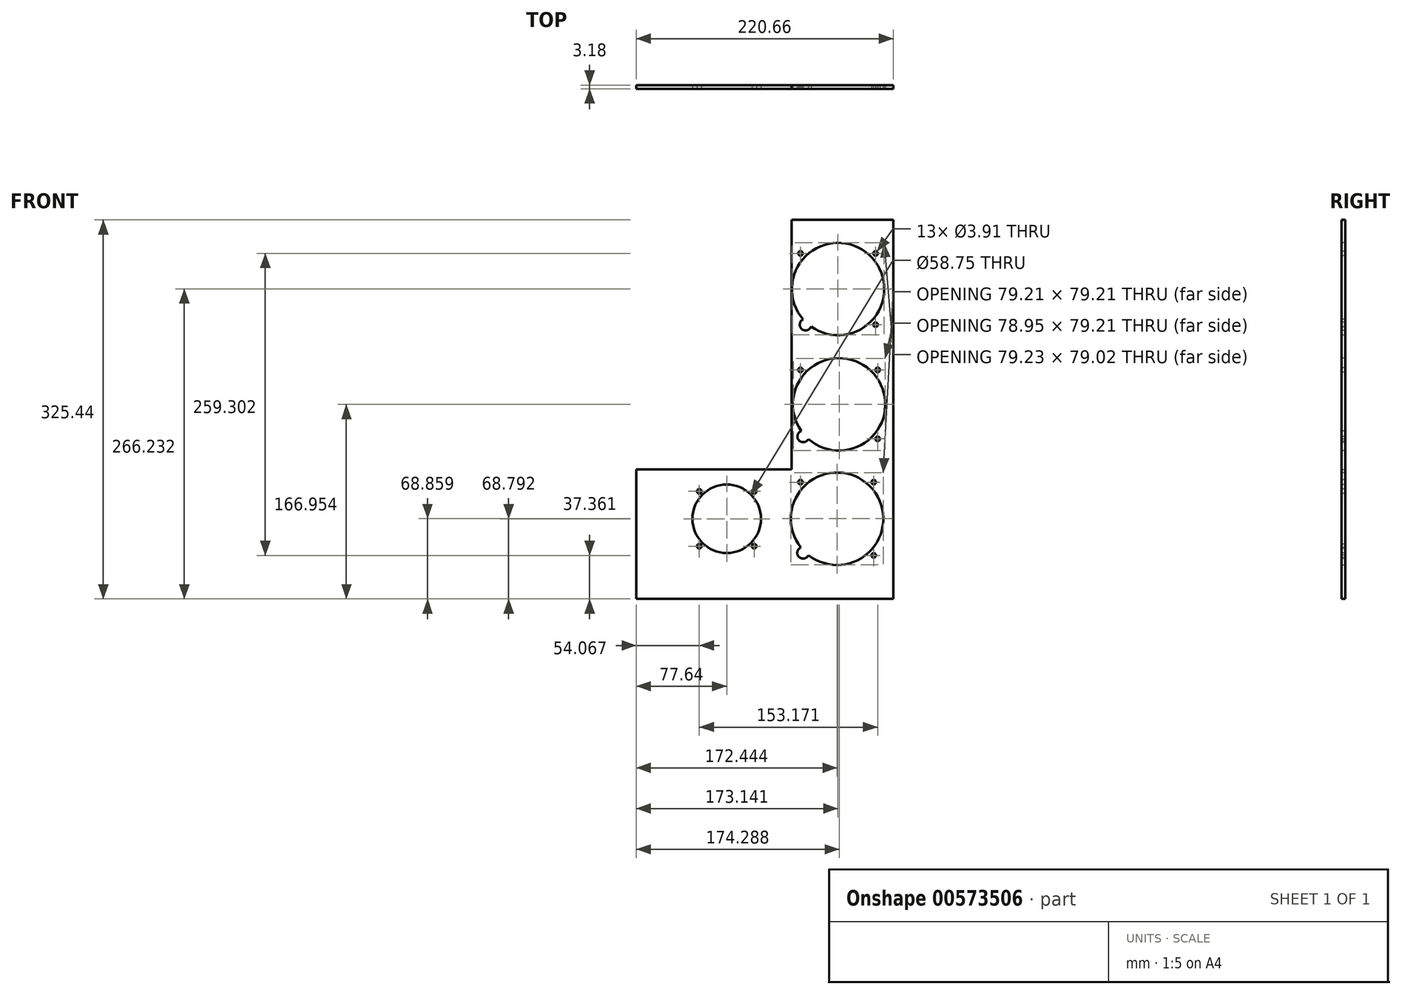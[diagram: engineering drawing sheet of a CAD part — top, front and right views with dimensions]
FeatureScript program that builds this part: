
annotation { "Feature Type Name" : "Feature", "Feature Type Description" : "" }
export const myFeature = defineFeature(function(context is Context, id is Id, definition is map)
    precondition{}
    {
        {
            var Q0;
            Q0=qCreatedBy(makeId("Front.planeOp"),FACE);
            var sketch = newSketch(context, id + "F0", { "sketchPlane" : qUnion([Q0])});
            skLineSegment(sketch, "E0", {"start": v(279.4, 0) * mm, "end": v(500.06, 0) * mm});
            skLineSegment(sketch, "E1", {"start": v(500.06, 0) * mm, "end": v(500.06, 325.44) * mm});
            skLineSegment(sketch, "E2", {"start": v(500.06, 325.44) * mm, "end": v(412.75, 325.44) * mm});
            skLineSegment(sketch, "E3", {"start": v(412.75, 325.44) * mm, "end": v(412.75, 111.13) * mm});
            skLineSegment(sketch, "E4", {"start": v(412.75, 111.13) * mm, "end": v(279.4, 111.13) * mm});
            skLineSegment(sketch, "E5", {"start": v(279.4, 111.12) * mm, "end": v(279.4, 0) * mm});
            skSolve(sketch);
        }
        {
            assignVariable(context, id + "F1", {"name" : "PanelThickness", "anyValue" : 3.17 * mm});
        }
        {
            var Q0;
            Q0=makeQuery(id+"F0.imprint","IMPRINT",FACE,{"disambiguationData":[TD([[makeQuery(id+"F0.imprint","IMPRINT",EDGE,{"derivedFrom":sQuery(id+"F0.wireOp",EDGE,"E0")}),1.0]])]});
            extrude(context, id + "F2", {"entities" : qUnion([Q0]), "depth" : (getVariable(context, 'PanelThickness')), "offsetDistance" : 25.4 * mm});
        }
        {
            var Q0;
            Q0=makeQuery(id+"F2.opExtrude","CAP_FACE",FACE,{"disambiguationData":[OSD([sQuery(id+"F0.wireOp",EDGE,"E0"),sQuery(id+"F0.wireOp",EDGE,"E1"),sQuery(id+"F0.wireOp",EDGE,"E2"),sQuery(id+"F0.wireOp",EDGE,"E3"),sQuery(id+"F0.wireOp",EDGE,"E4"),sQuery(id+"F0.wireOp",EDGE,"E5")])],"isStart":false});
            var sketch = newSketch(context, id + "F3", { "sketchPlane" : qUnion([Q0])});
            skCircle(sketch, "E6", {"center": v(452.58, 266.06) * mm, "radius": 39.69 * mm});
            skCircle(sketch, "E7.2.0.0", {"center": v(420.35, 296.66) * mm, "radius": 1.96 * mm});
            skCircle(sketch, "E7.2.0.1", {"center": v(484.82, 296.66) * mm, "radius": 1.96 * mm});
            skCircle(sketch, "E7.2.0.2", {"center": v(484.82, 235.45) * mm, "radius": 1.96 * mm});
            skLineSegment(sketch, "E8", {"start": v(484.82, 296.66) * mm, "end": v(424.73, 235.45) * mm});
            skCircle(sketch, "E9", {"center": v(424.73, 235.45) * mm, "radius": 4.97 * mm});
            skLineSegment(sketch, "E10", {"start": v(420.35, 296.66) * mm, "end": v(484.82, 235.45) * mm});
            skCircle(sketch, "E11", {"center": v(453.5, 167.02) * mm, "radius": 39.69 * mm});
            skCircle(sketch, "E12.2.0.0", {"center": v(420.35, 196.63) * mm, "radius": 1.96 * mm});
            skCircle(sketch, "E12.2.0.1", {"center": v(486.64, 196.63) * mm, "radius": 1.96 * mm});
            skCircle(sketch, "E12.2.0.2", {"center": v(486.64, 137.4) * mm, "radius": 1.96 * mm});
            skLineSegment(sketch, "E13", {"start": v(486.64, 196.63) * mm, "end": v(422.68, 139.48) * mm});
            skCircle(sketch, "E14", {"center": v(422.68, 139.48) * mm, "radius": 4.97 * mm});
            skLineSegment(sketch, "E15", {"start": v(420.35, 196.63) * mm, "end": v(486.64, 137.4) * mm});
            skCircle(sketch, "E16", {"center": v(451.78, 68.8) * mm, "radius": 39.69 * mm});
            skCircle(sketch, "E17.2.0.0", {"center": v(420.35, 100.22) * mm, "radius": 1.96 * mm});
            skCircle(sketch, "E17.2.0.1", {"center": v(483.2, 100.22) * mm, "radius": 1.96 * mm});
            skCircle(sketch, "E17.2.0.2", {"center": v(483.2, 37.36) * mm, "radius": 1.96 * mm});
            skLineSegment(sketch, "E18", {"start": v(483.2, 100.22) * mm, "end": v(422.56, 39.57) * mm});
            skCircle(sketch, "E19", {"center": v(422.56, 39.57) * mm, "radius": 4.97 * mm});
            skLineSegment(sketch, "E20", {"start": v(420.35, 100.22) * mm, "end": v(483.2, 37.36) * mm});
            skCircle(sketch, "E21", {"center": v(357.04, 68.8) * mm, "radius": 29.38 * mm});
            skCircle(sketch, "E22", {"center": v(333.47, 92.37) * mm, "radius": 1.96 * mm});
            skCircle(sketch, "E23", {"center": v(380.61, 92.37) * mm, "radius": 1.96 * mm});
            skCircle(sketch, "E24", {"center": v(380.61, 45.22) * mm, "radius": 1.96 * mm});
            skCircle(sketch, "E25", {"center": v(333.47, 45.22) * mm, "radius": 1.96 * mm});
            skLineSegment(sketch, "E26", {"start": v(333.47, 92.37) * mm, "end": v(380.61, 45.22) * mm});
            skLineSegment(sketch, "E27", {"start": v(380.61, 92.37) * mm, "end": v(333.47, 45.22) * mm});
            skSolve(sketch);
        }
        {
            var Q0;
            Q0 = qSketchRegion(id + "F3", true);
            extrude(context, id + "F4", {"entities" : qUnion([Q0]), "operationType" : NewBodyOperationType.REMOVE, "oppositeDirection" : true, "depth" : (getVariable(context, 'PanelThickness')), "offsetDistance" : 25.4 * mm});
        }
    });
